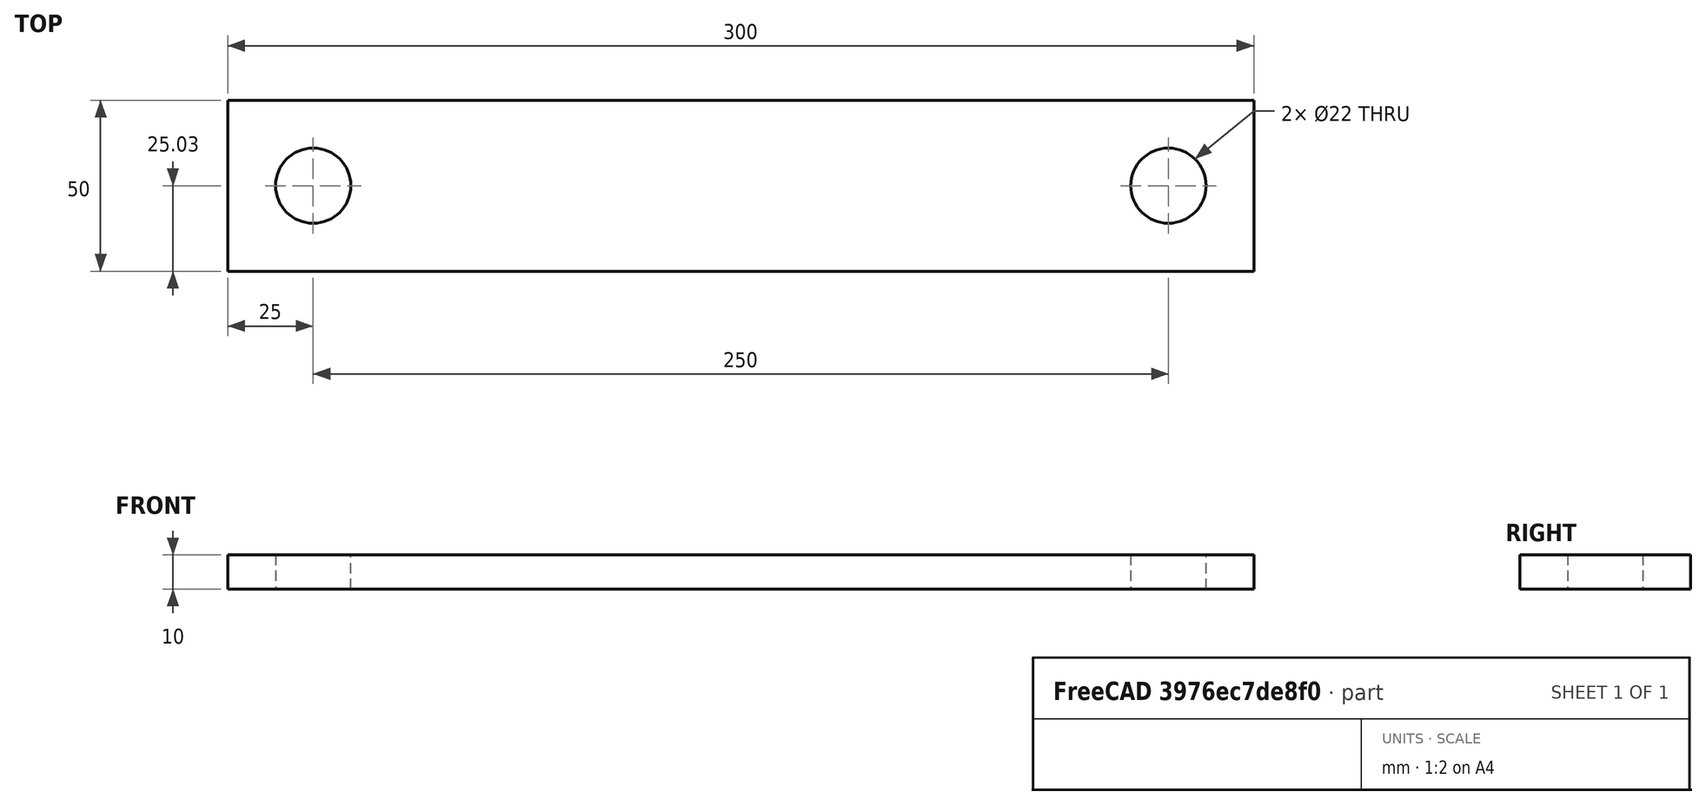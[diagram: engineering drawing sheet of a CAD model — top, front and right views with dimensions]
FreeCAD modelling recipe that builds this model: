
FCSTD DOCUMENT  (FreeCAD 0.19R24276 (Git))
Label: Richag_L300_2podshipniks
License: All rights reserved
LicenseURL: http://en.wikipedia.org/wiki/All_rights_reserved
objects: Sketcher::SketchObject×1, PartDesign::Pad×1, PartDesign::Body×1
note: 4 computed .brp shape members not serialized (recipe doc carries the construction recipe); baked Part::Feature solids carry a one-line shape summary decoded from their .brp

FEATURE [Sketcher::SketchObject] Sketch
  FullyConstrained = false
  MapMode = 5
  Support = -> [XY_Plane]
  sketch-geometry (6):
    g0: Circle CenterX=0 CenterY=0 CenterZ=0 NormalX=0 NormalY=0 NormalZ=1 AngleXU=0 Radius=11
    g1: LineSegment StartX=-25 StartY=24.9744 StartZ=0 EndX=275 EndY=24.9744 EndZ=0
    g2: LineSegment StartX=-25 StartY=-25.0256 StartZ=0 EndX=-25 EndY=24.9744 EndZ=0
    g3: Circle CenterX=250 CenterY=0 CenterZ=0 NormalX=0 NormalY=0 NormalZ=1 AngleXU=0 Radius=11
    g4: LineSegment StartX=275 StartY=24.9744 StartZ=0 EndX=275 EndY=-25.0256 EndZ=0
    g5: LineSegment StartX=-25 StartY=-25.0256 StartZ=0 EndX=275 EndY=-25.0256 EndZ=0
  constraints (15):
    c: Diameter(g0) = 22
    c: Coincident(g2,g1)
    c: Horizontal(g1)
    c: Vertical(g2)
    c: Distance(g2) = 50
    c: DistanceX(g1,g0) = 25
    c: DistanceX(g1,g1) = 300
    c: Diameter(g3) = 22
    c: Coincident(g0,g-1)
    c: Coincident(g4,g1)
    c: Vertical(g4)
    c: Coincident(g5,g2)
    c: Coincident(g5,g4)
    c: Horizontal(g5)
    c: DistanceX(g0,g3) = 250
FEATURE [PartDesign::Pad] Pad
  Direction = (1,1,1)
  Length = 10
  Length2 = 100
  Profile = -> Sketch
  Type = 0
FEATURE [PartDesign::Body] Body
  Group = -> [Sketch,Pad]
  Origin = -> Origin
  Tip = -> Pad
